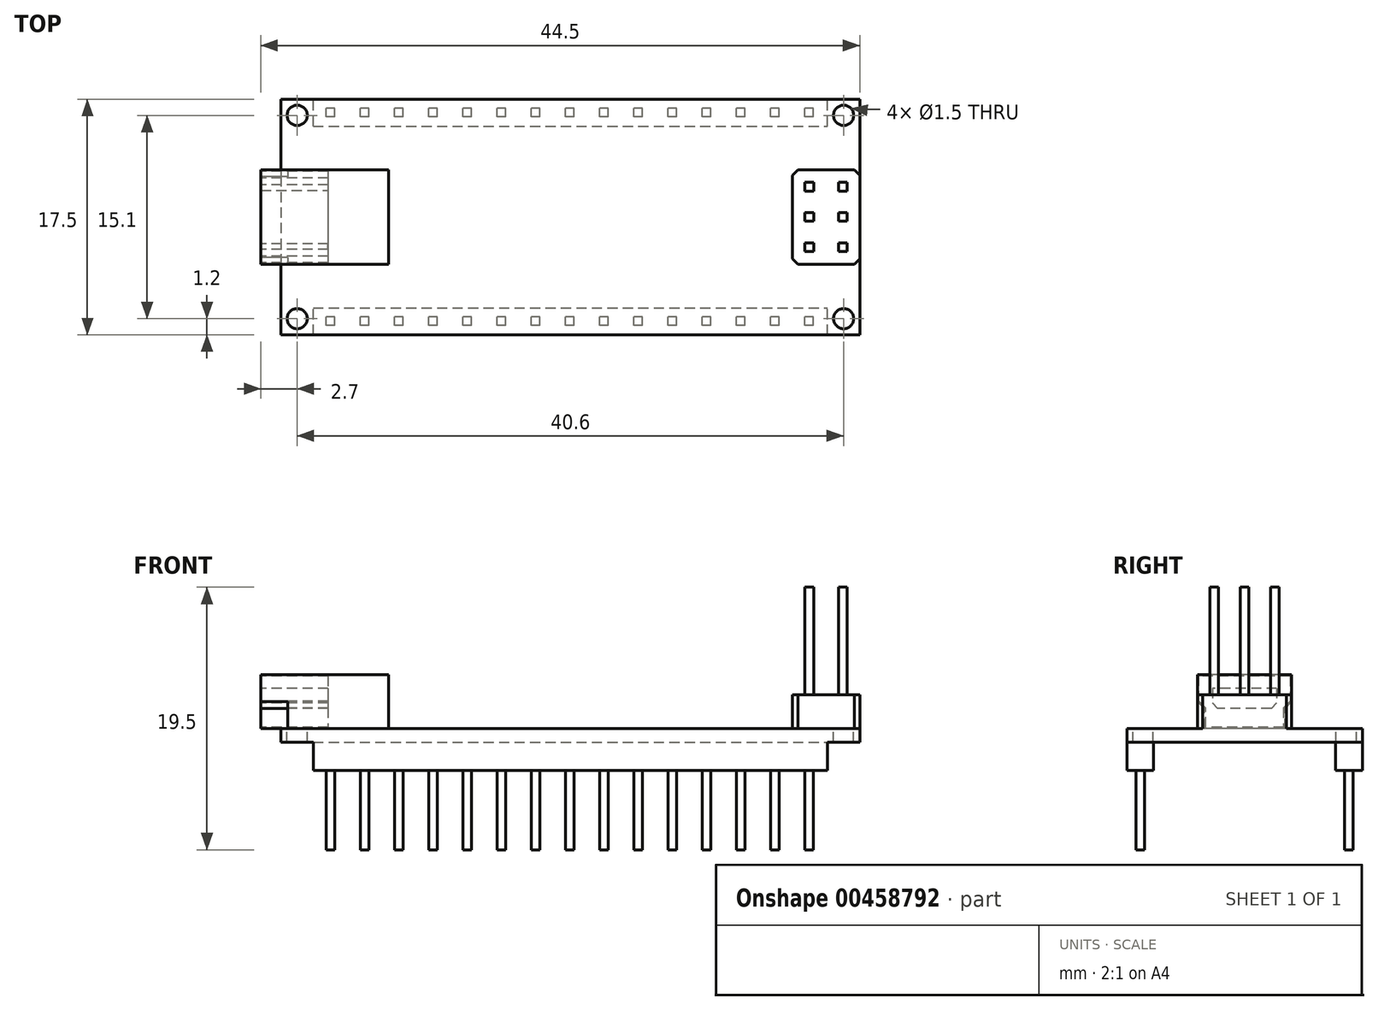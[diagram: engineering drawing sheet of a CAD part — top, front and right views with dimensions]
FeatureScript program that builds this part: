
annotation { "Feature Type Name" : "Feature", "Feature Type Description" : "" }
export const myFeature = defineFeature(function(context is Context, id is Id, definition is map)
    precondition{}
    {
        {
            var Q0;
            Q0=qCreatedBy(makeId("Top.planeOp"),FACE);
            var sketch = newSketch(context, id + "F0", { "sketchPlane" : qUnion([Q0])});
            skLineSegment(sketch, "E0.bottom", {"start": v(21.5, 8.75) * mm, "end": v(-21.5, 8.75) * mm});
            skLineSegment(sketch, "E0.top", {"start": v(21.5, -8.75) * mm, "end": v(-21.5, -8.75) * mm});
            skLineSegment(sketch, "E0.left", {"start": v(21.5, 8.75) * mm, "end": v(21.5, -8.75) * mm});
            skLineSegment(sketch, "E0.right", {"start": v(-21.5, 8.75) * mm, "end": v(-21.5, -8.75) * mm});
            skPoint(sketch, "E0.middle", {"position": v(0, 0) * mm});
            skCircle(sketch, "E1", {"center": v(-20.3, 7.55) * mm, "radius": 0.75 * mm});
            skCircle(sketch, "E2.0.1.0", {"center": v(-20.3, -7.55) * mm, "radius": 0.75 * mm});
            skCircle(sketch, "E2.1.0.0", {"center": v(20.3, 7.55) * mm, "radius": 0.75 * mm});
            skCircle(sketch, "E2.1.1.0", {"center": v(20.3, -7.55) * mm, "radius": 0.75 * mm});
            skLineSegment(sketch, "E2.direction1", {"start": v(-20.3, 7.55) * mm, "end": v(20.3, 7.55) * mm, "construction": true});
            skLineSegment(sketch, "E2.direction2", {"start": v(-20.3, 7.55) * mm, "end": v(-20.3, -7.55) * mm, "construction": true});
            skPoint(sketch, "E3", {"position": v(21.5, 0) * mm});
            skPoint(sketch, "E4", {"position": v(-21.5, 0) * mm});
            skLineSegment(sketch, "E5.bottom", {"start": v(-23, 3.5) * mm, "end": v(-13.5, 3.5) * mm});
            skLineSegment(sketch, "E5.top", {"start": v(-23, -3.5) * mm, "end": v(-13.5, -3.5) * mm});
            skLineSegment(sketch, "E5.left", {"start": v(-23, 3.5) * mm, "end": v(-23, -3.5) * mm});
            skLineSegment(sketch, "E5.right", {"start": v(-13.5, 3.5) * mm, "end": v(-13.5, -3.5) * mm});
            skPoint(sketch, "E6", {"position": v(-13.5, 0) * mm});
            skLineSegment(sketch, "E7.bottom", {"start": v(21.5, 3.5) * mm, "end": v(16.5, 3.5) * mm});
            skLineSegment(sketch, "E7.top", {"start": v(21.5, -3.5) * mm, "end": v(16.5, -3.5) * mm});
            skLineSegment(sketch, "E7.left", {"start": v(21.5, 3.5) * mm, "end": v(21.5, -3.5) * mm});
            skLineSegment(sketch, "E7.right", {"start": v(16.5, 3.5) * mm, "end": v(16.5, -3.5) * mm});
            skSolve(sketch);
        }
        {
            var Q0;
            {var subQ5=sQuery(id+"F0.wireOp",EDGE,"E5.right");Q0=makeQuery(id+"F0.imprint","IMPRINT",FACE,{"disambiguationData":[TD([[makeQuery(id+"F0.imprint","IMPRINT",EDGE,{"derivedFrom":subQ5}),-1.0]])]});}
            var Q1;
            {var subQ0=sQuery(id+"F0.wireOp",EDGE,"E0.bottom");Q1=makeQuery(id+"F0.imprint","IMPRINT",FACE,{"disambiguationData":[TD([[makeQuery(id+"F0.imprint","IMPRINT",EDGE,{"derivedFrom":subQ0}),1.0]])]});}
            var Q2;
            Q2=makeQuery(id+"F0.imprint","IMPRINT",FACE,{"disambiguationData":[TD([[makeQuery(id+"F0.imprint","IMPRINT",EDGE,{"derivedFrom":sQuery(id+"F0.wireOp",EDGE,"E7.bottom")}),1.0]])]});
            extrude(context, id + "F1", {"entities" : qUnion([Q0, Q1, Q2]), "oppositeDirection" : true, "depth" : 1 * mm});
        }
        {
            var Q0;
            {var subQ5=sQuery(id+"F0.wireOp",EDGE,"E5.left");Q0=makeQuery(id+"F0.imprint","IMPRINT",FACE,{"disambiguationData":[TD([[makeQuery(id+"F0.imprint","IMPRINT",EDGE,{"derivedFrom":subQ5}),1.0]])]});}
            var Q1;
            {var subQ5=sQuery(id+"F0.wireOp",EDGE,"E5.right");Q1=makeQuery(id+"F0.imprint","IMPRINT",FACE,{"disambiguationData":[TD([[makeQuery(id+"F0.imprint","IMPRINT",EDGE,{"derivedFrom":subQ5}),-1.0]])]});}
            extrude(context, id + "F2", {"entities" : qUnion([Q0, Q1]), "operationType" : NewBodyOperationType.ADD, "depth" : 4 * mm});
        }
        {
            var Q0;
            Q0=makeQuery(id+"F0.imprint","IMPRINT",FACE,{"disambiguationData":[TD([[makeQuery(id+"F0.imprint","IMPRINT",EDGE,{"derivedFrom":sQuery(id+"F0.wireOp",EDGE,"E7.bottom")}),1.0]])]});
            extrude(context, id + "F3", {"entities" : qUnion([Q0]), "operationType" : NewBodyOperationType.ADD, "depth" : 2.5 * mm});
        }
        {
            var Q0;
            Q0=makeQuery(id+"F2.opExtrude","SWEPT_FACE",FACE,{"disambiguationData":[OSD([sQuery(id+"F0.wireOp",EDGE,"E5.left")])]});
            var sketch = newSketch(context, id + "F4", { "sketchPlane" : qUnion([Q0])});
            skPoint(sketch, "E8", {"position": v(-3.5, 2) * mm});
            skPoint(sketch, "E9", {"position": v(3.5, 2) * mm});
            skPoint(sketch, "E10", {"position": v(-3, 0) * mm});
            skPoint(sketch, "E11", {"position": v(3, 0) * mm});
            skPoint(sketch, "E12", {"position": v(-3, 1.5) * mm});
            skPoint(sketch, "E13", {"position": v(3, 1.5) * mm});
            skLineSegment(sketch, "E14", {"start": v(-3.5, 2) * mm, "end": v(-3, 1.5) * mm});
            skLineSegment(sketch, "E15", {"start": v(-3, 0) * mm, "end": v(-3, 1.5) * mm});
            skLineSegment(sketch, "E16", {"start": v(3, 0) * mm, "end": v(3, 1.5) * mm});
            skLineSegment(sketch, "E17", {"start": v(3, 1.5) * mm, "end": v(3.5, 2) * mm});
            skLineSegment(sketch, "E18.bottom", {"start": v(-2.4, 3) * mm, "end": v(2.4, 3) * mm});
            skLineSegment(sketch, "E18.top", {"start": v(-2.4, 1.5) * mm, "end": v(2.4, 1.5) * mm});
            skLineSegment(sketch, "E18.left", {"start": v(-2.4, 3) * mm, "end": v(-2.4, 1.5) * mm});
            skLineSegment(sketch, "E18.right", {"start": v(2.4, 3) * mm, "end": v(2.4, 1.5) * mm});
            skPoint(sketch, "E19", {"position": v(0, 3) * mm});
            skPoint(sketch, "E20", {"position": v(-2.4, 2.25) * mm});
            skPoint(sketch, "E21", {"position": v(-3.5, 4) * mm});
            skPoint(sketch, "E22", {"position": v(3.5, 4) * mm});
            skLineSegment(sketch, "E23.0", {"start": v(-3.5, -1) * mm, "end": v(3.5, -1) * mm});
            skLineSegment(sketch, "E24", {"start": v(-3.5, 4) * mm, "end": v(-3.5, 2) * mm});
            skLineSegment(sketch, "E25", {"start": v(-3, 1.5) * mm, "end": v(-3, 0) * mm});
            skLineSegment(sketch, "E26", {"start": v(-3, 0) * mm, "end": v(3, 0) * mm});
            skLineSegment(sketch, "E27", {"start": v(3.5, 2) * mm, "end": v(3.5, 4) * mm});
            skLineSegment(sketch, "E28.0", {"start": v(-3.4, 3.9) * mm, "end": v(3.4, 3.9) * mm});
            skLineSegment(sketch, "E28.1", {"start": v(3.4, 2.04) * mm, "end": v(3.4, 3.9) * mm});
            skLineSegment(sketch, "E28.2", {"start": v(-3.4, 3.9) * mm, "end": v(-3.4, 2.04) * mm});
            skLineSegment(sketch, "E28.3", {"start": v(2.9, 1.54) * mm, "end": v(3.4, 2.04) * mm});
            skLineSegment(sketch, "E28.4", {"start": v(-3.4, 2.04) * mm, "end": v(-2.9, 1.54) * mm});
            skLineSegment(sketch, "E28.5", {"start": v(-2.9, 1.54) * mm, "end": v(-2.9, 0.1) * mm});
            skLineSegment(sketch, "E28.6", {"start": v(-2.9, 0.1) * mm, "end": v(2.9, 0.1) * mm});
            skLineSegment(sketch, "E28.7", {"start": v(2.9, 0.1) * mm, "end": v(2.9, 1.54) * mm});
            skPoint(sketch, "E29", {"position": v(-3.4, 2.04) * mm});
            skPoint(sketch, "E30", {"position": v(-2.9, 1.54) * mm});
            skSolve(sketch);
        }
        {
            var Q0;
            Q0=makeQuery(id+"F4.imprint","IMPRINT",FACE,{"disambiguationData":[TD([[makeQuery(id+"F4.imprint","IMPRINT",EDGE,{"derivedFrom":sQuery(id+"F4.wireOp",EDGE,"E18.bottom")}),1.0]])]});
            extrude(context, id + "F5", {"entities" : qUnion([Q0]), "operationType" : NewBodyOperationType.REMOVE, "oppositeDirection" : true, "depth" : 5 * mm});
        }
        {
            var Q0;
            {var subQ0=sQuery(id+"F4.wireOp",EDGE,"E14");Q0=makeQuery(id+"F4.imprint","IMPRINT",FACE,{"disambiguationData":[TD([[makeQuery(id+"F4.imprint","IMPRINT",EDGE,{"derivedFrom":subQ0}),-1.0]])]});}
            var Q1;
            {var subQ0=sQuery(id+"F4.wireOp",EDGE,"E16");Q1=makeQuery(id+"F4.imprint","IMPRINT",FACE,{"disambiguationData":[TD([[makeQuery(id+"F4.imprint","IMPRINT",EDGE,{"derivedFrom":subQ0}),-1.0]])]});}
            extrude(context, id + "F6", {"entities" : qUnion([Q0, Q1]), "operationType" : NewBodyOperationType.REMOVE, "oppositeDirection" : true, "depth" : 2 * mm});
        }
        {
            var Q0;
            Q0=makeQuery(id+"F1.opExtrude","CAP_FACE",FACE,{"disambiguationData":[OSD([sQuery(id+"F0.wireOp",EDGE,"E0.bottom"),sQuery(id+"F0.wireOp",EDGE,"E0.top"),sQuery(id+"F0.wireOp",EDGE,"E0.left"),sQuery(id+"F0.wireOp",EDGE,"E0.right"),sQuery(id+"F0.wireOp",EDGE,"E1"),sQuery(id+"F0.wireOp",EDGE,"E2.0.1.0"),sQuery(id+"F0.wireOp",EDGE,"E2.1.0.0"),sQuery(id+"F0.wireOp",EDGE,"E2.1.1.0"),sQuery(id+"F0.wireOp",EDGE,"E7.left")])],"isStart":false});
            var sketch = newSketch(context, id + "F7", { "sketchPlane" : qUnion([Q0])});
            skLineSegment(sketch, "E31.bottom", {"start": v(-19.1, 8.75) * mm, "end": v(19.1, 8.75) * mm});
            skLineSegment(sketch, "E31.top", {"start": v(-19.1, 6.75) * mm, "end": v(19.1, 6.75) * mm});
            skLineSegment(sketch, "E31.left", {"start": v(-19.1, 8.75) * mm, "end": v(-19.1, 6.75) * mm});
            skLineSegment(sketch, "E31.right", {"start": v(19.1, 8.75) * mm, "end": v(19.1, 6.75) * mm});
            skPoint(sketch, "E32", {"position": v(0, 6.75) * mm});
            skLineSegment(sketch, "E33", {"start": v(-19.1, 7.75) * mm, "end": v(19.1, 7.75) * mm, "construction": true});
            skPoint(sketch, "E34", {"position": v(-17.83, 7.75) * mm});
            skLineSegment(sketch, "E35.bottom", {"start": v(-17.51, 8.07) * mm, "end": v(-18.15, 8.07) * mm});
            skLineSegment(sketch, "E35.top", {"start": v(-17.51, 7.43) * mm, "end": v(-18.15, 7.43) * mm});
            skLineSegment(sketch, "E35.left", {"start": v(-17.51, 8.07) * mm, "end": v(-17.51, 7.43) * mm});
            skLineSegment(sketch, "E35.right", {"start": v(-18.15, 8.07) * mm, "end": v(-18.15, 7.43) * mm});
            skPoint(sketch, "E36.1.0.0", {"position": v(-15.3, 7.75) * mm});
            skLineSegment(sketch, "E36.1.0.1", {"start": v(-14.97, 8.07) * mm, "end": v(-14.97, 7.43) * mm});
            skLineSegment(sketch, "E36.1.0.2", {"start": v(-14.97, 8.07) * mm, "end": v(-15.61, 8.07) * mm});
            skLineSegment(sketch, "E36.1.0.3", {"start": v(-15.61, 8.07) * mm, "end": v(-15.61, 7.43) * mm});
            skLineSegment(sketch, "E36.1.0.4", {"start": v(-14.97, 7.43) * mm, "end": v(-15.61, 7.43) * mm});
            skPoint(sketch, "E36.2.0.0", {"position": v(-12.75, 7.75) * mm});
            skLineSegment(sketch, "E36.2.0.1", {"start": v(-12.43, 8.07) * mm, "end": v(-12.43, 7.43) * mm});
            skLineSegment(sketch, "E36.2.0.2", {"start": v(-12.43, 8.07) * mm, "end": v(-13.07, 8.07) * mm});
            skLineSegment(sketch, "E36.2.0.3", {"start": v(-13.07, 8.07) * mm, "end": v(-13.07, 7.43) * mm});
            skLineSegment(sketch, "E36.2.0.4", {"start": v(-12.43, 7.43) * mm, "end": v(-13.07, 7.43) * mm});
            skPoint(sketch, "E36.3.0.0", {"position": v(-10.21, 7.75) * mm});
            skLineSegment(sketch, "E36.3.0.1", {"start": v(-9.89, 8.07) * mm, "end": v(-9.89, 7.43) * mm});
            skLineSegment(sketch, "E36.3.0.2", {"start": v(-9.89, 8.07) * mm, "end": v(-10.53, 8.07) * mm});
            skLineSegment(sketch, "E36.3.0.3", {"start": v(-10.53, 8.07) * mm, "end": v(-10.53, 7.43) * mm});
            skLineSegment(sketch, "E36.3.0.4", {"start": v(-9.89, 7.43) * mm, "end": v(-10.53, 7.43) * mm});
            skPoint(sketch, "E36.4.0.0", {"position": v(-7.67, 7.75) * mm});
            skLineSegment(sketch, "E36.4.0.1", {"start": v(-7.35, 8.07) * mm, "end": v(-7.35, 7.43) * mm});
            skLineSegment(sketch, "E36.4.0.2", {"start": v(-7.35, 8.07) * mm, "end": v(-8, 8.07) * mm});
            skLineSegment(sketch, "E36.4.0.3", {"start": v(-8, 8.07) * mm, "end": v(-8, 7.43) * mm});
            skLineSegment(sketch, "E36.4.0.4", {"start": v(-7.35, 7.43) * mm, "end": v(-8, 7.43) * mm});
            skPoint(sketch, "E36.5.0.0", {"position": v(-5.13, 7.75) * mm});
            skLineSegment(sketch, "E36.5.0.1", {"start": v(-4.8, 8.07) * mm, "end": v(-4.8, 7.43) * mm});
            skLineSegment(sketch, "E36.5.0.2", {"start": v(-4.8, 8.07) * mm, "end": v(-5.45, 8.07) * mm});
            skLineSegment(sketch, "E36.5.0.3", {"start": v(-5.45, 8.07) * mm, "end": v(-5.45, 7.43) * mm});
            skLineSegment(sketch, "E36.5.0.4", {"start": v(-4.8, 7.43) * mm, "end": v(-5.45, 7.43) * mm});
            skPoint(sketch, "E36.6.0.0", {"position": v(-2.59, 7.75) * mm});
            skLineSegment(sketch, "E36.6.0.1", {"start": v(-2.27, 8.07) * mm, "end": v(-2.27, 7.43) * mm});
            skLineSegment(sketch, "E36.6.0.2", {"start": v(-2.27, 8.07) * mm, "end": v(-2.9, 8.07) * mm});
            skLineSegment(sketch, "E36.6.0.3", {"start": v(-2.9, 8.07) * mm, "end": v(-2.9, 7.43) * mm});
            skLineSegment(sketch, "E36.6.0.4", {"start": v(-2.27, 7.43) * mm, "end": v(-2.9, 7.43) * mm});
            skPoint(sketch, "E36.7.0.0", {"position": v(-0.05, 7.75) * mm});
            skLineSegment(sketch, "E36.7.0.1", {"start": v(0.27, 8.07) * mm, "end": v(0.27, 7.43) * mm});
            skLineSegment(sketch, "E36.7.0.2", {"start": v(0.27, 8.07) * mm, "end": v(-0.37, 8.07) * mm});
            skLineSegment(sketch, "E36.7.0.3", {"start": v(-0.37, 8.07) * mm, "end": v(-0.37, 7.43) * mm});
            skLineSegment(sketch, "E36.7.0.4", {"start": v(0.27, 7.43) * mm, "end": v(-0.37, 7.43) * mm});
            skPoint(sketch, "E36.8.0.0", {"position": v(2.5, 7.75) * mm});
            skLineSegment(sketch, "E36.8.0.1", {"start": v(2.81, 8.07) * mm, "end": v(2.81, 7.43) * mm});
            skLineSegment(sketch, "E36.8.0.2", {"start": v(2.81, 8.07) * mm, "end": v(2.17, 8.07) * mm});
            skLineSegment(sketch, "E36.8.0.3", {"start": v(2.17, 8.07) * mm, "end": v(2.17, 7.43) * mm});
            skLineSegment(sketch, "E36.8.0.4", {"start": v(2.81, 7.43) * mm, "end": v(2.17, 7.43) * mm});
            skPoint(sketch, "E36.9.0.0", {"position": v(5.03, 7.75) * mm});
            skLineSegment(sketch, "E36.9.0.1", {"start": v(5.35, 8.07) * mm, "end": v(5.35, 7.43) * mm});
            skLineSegment(sketch, "E36.9.0.2", {"start": v(5.35, 8.07) * mm, "end": v(4.71, 8.07) * mm});
            skLineSegment(sketch, "E36.9.0.3", {"start": v(4.71, 8.07) * mm, "end": v(4.71, 7.43) * mm});
            skLineSegment(sketch, "E36.9.0.4", {"start": v(5.35, 7.43) * mm, "end": v(4.71, 7.43) * mm});
            skPoint(sketch, "E36.10.0.0", {"position": v(7.57, 7.75) * mm});
            skLineSegment(sketch, "E36.10.0.1", {"start": v(7.9, 8.07) * mm, "end": v(7.9, 7.43) * mm});
            skLineSegment(sketch, "E36.10.0.2", {"start": v(7.9, 8.07) * mm, "end": v(7.25, 8.07) * mm});
            skLineSegment(sketch, "E36.10.0.3", {"start": v(7.25, 8.07) * mm, "end": v(7.25, 7.43) * mm});
            skLineSegment(sketch, "E36.10.0.4", {"start": v(7.9, 7.43) * mm, "end": v(7.25, 7.43) * mm});
            skPoint(sketch, "E36.11.0.0", {"position": v(10.11, 7.75) * mm});
            skLineSegment(sketch, "E36.11.0.1", {"start": v(10.43, 8.07) * mm, "end": v(10.43, 7.43) * mm});
            skLineSegment(sketch, "E36.11.0.2", {"start": v(10.43, 8.07) * mm, "end": v(9.8, 8.07) * mm});
            skLineSegment(sketch, "E36.11.0.3", {"start": v(9.8, 8.07) * mm, "end": v(9.8, 7.43) * mm});
            skLineSegment(sketch, "E36.11.0.4", {"start": v(10.43, 7.43) * mm, "end": v(9.8, 7.43) * mm});
            skPoint(sketch, "E36.12.0.0", {"position": v(12.65, 7.75) * mm});
            skLineSegment(sketch, "E36.12.0.1", {"start": v(12.97, 8.07) * mm, "end": v(12.97, 7.43) * mm});
            skLineSegment(sketch, "E36.12.0.2", {"start": v(12.97, 8.07) * mm, "end": v(12.33, 8.07) * mm});
            skLineSegment(sketch, "E36.12.0.3", {"start": v(12.33, 8.07) * mm, "end": v(12.33, 7.43) * mm});
            skLineSegment(sketch, "E36.12.0.4", {"start": v(12.97, 7.43) * mm, "end": v(12.33, 7.43) * mm});
            skPoint(sketch, "E36.13.0.0", {"position": v(15.2, 7.75) * mm});
            skLineSegment(sketch, "E36.13.0.1", {"start": v(15.51, 8.07) * mm, "end": v(15.51, 7.43) * mm});
            skLineSegment(sketch, "E36.13.0.2", {"start": v(15.51, 8.07) * mm, "end": v(14.87, 8.07) * mm});
            skLineSegment(sketch, "E36.13.0.3", {"start": v(14.87, 8.07) * mm, "end": v(14.87, 7.43) * mm});
            skLineSegment(sketch, "E36.13.0.4", {"start": v(15.51, 7.43) * mm, "end": v(14.87, 7.43) * mm});
            skPoint(sketch, "E36.14.0.0", {"position": v(17.73, 7.75) * mm});
            skLineSegment(sketch, "E36.14.0.1", {"start": v(18.05, 8.07) * mm, "end": v(18.05, 7.43) * mm});
            skLineSegment(sketch, "E36.14.0.2", {"start": v(18.05, 8.07) * mm, "end": v(17.41, 8.07) * mm});
            skLineSegment(sketch, "E36.14.0.3", {"start": v(17.41, 8.07) * mm, "end": v(17.41, 7.43) * mm});
            skLineSegment(sketch, "E36.14.0.4", {"start": v(18.05, 7.43) * mm, "end": v(17.41, 7.43) * mm});
            skLineSegment(sketch, "E36.direction1", {"start": v(-17.83, 7.75) * mm, "end": v(-15.3, 7.75) * mm, "construction": true});
            skPoint(sketch, "E37", {"position": v(-20.3, 7.55) * mm});
            skLineSegment(sketch, "E38", {"start": v(-20.3, 7.55) * mm, "end": v(-21.5, 7.55) * mm});
            skLineSegment(sketch, "E39", {"start": v(-21.5, 7.55) * mm, "end": v(-19.1, 7.55) * mm});
            skPoint(sketch, "E40", {"position": v(-21.05, 7.55) * mm});
            skPoint(sketch, "E41", {"position": v(-19.55, 7.55) * mm});
            skPoint(sketch, "E42", {"position": v(20.3, 7.55) * mm});
            skLineSegment(sketch, "E43", {"start": v(20.3, 7.55) * mm, "end": v(21.5, 7.55) * mm});
            skLineSegment(sketch, "E44", {"start": v(21.5, 7.55) * mm, "end": v(19.1, 7.55) * mm});
            skPoint(sketch, "E45", {"position": v(21.05, 7.55) * mm});
            skPoint(sketch, "E46", {"position": v(19.55, 7.55) * mm});
            skPoint(sketch, "E47.0.1.0", {"position": v(-0.05, -7.75) * mm});
            skPoint(sketch, "E47.0.1.1", {"position": v(-5.13, -7.75) * mm});
            skPoint(sketch, "E47.0.1.2", {"position": v(12.65, -7.75) * mm});
            skPoint(sketch, "E47.0.1.3", {"position": v(-7.67, -7.75) * mm});
            skPoint(sketch, "E47.0.1.4", {"position": v(17.73, -7.75) * mm});
            skPoint(sketch, "E47.0.1.5", {"position": v(-10.21, -7.75) * mm});
            skPoint(sketch, "E47.0.1.6", {"position": v(7.57, -7.75) * mm});
            skPoint(sketch, "E47.0.1.7", {"position": v(2.49, -7.75) * mm});
            skPoint(sketch, "E47.0.1.8", {"position": v(0, -8.75) * mm});
            skPoint(sketch, "E47.0.1.9", {"position": v(-17.83, -7.75) * mm});
            skPoint(sketch, "E47.0.1.10", {"position": v(5.03, -7.75) * mm});
            skPoint(sketch, "E47.0.1.11", {"position": v(-15.3, -7.75) * mm});
            skLineSegment(sketch, "E47.0.1.12", {"start": v(-17.83, -7.75) * mm, "end": v(-15.3, -7.75) * mm, "construction": true});
            skPoint(sketch, "E47.0.1.13", {"position": v(10.11, -7.75) * mm});
            skPoint(sketch, "E47.0.1.14", {"position": v(15.2, -7.75) * mm});
            skPoint(sketch, "E47.0.1.15", {"position": v(-2.6, -7.75) * mm});
            skPoint(sketch, "E47.0.1.16", {"position": v(-12.75, -7.75) * mm});
            skPoint(sketch, "E47.0.1.17", {"position": v(-17.83, -7.75) * mm});
            skLineSegment(sketch, "E47.0.1.18", {"start": v(18.05, -7.43) * mm, "end": v(17.41, -7.43) * mm});
            skLineSegment(sketch, "E47.0.1.19", {"start": v(18.05, -8.07) * mm, "end": v(17.41, -8.07) * mm});
            skLineSegment(sketch, "E47.0.1.20", {"start": v(18.05, -7.43) * mm, "end": v(18.05, -8.07) * mm});
            skLineSegment(sketch, "E47.0.1.21", {"start": v(-0.37, -7.43) * mm, "end": v(-0.37, -8.07) * mm});
            skLineSegment(sketch, "E47.0.1.22", {"start": v(-10.53, -7.43) * mm, "end": v(-10.53, -8.07) * mm});
            skLineSegment(sketch, "E47.0.1.23", {"start": v(-9.89, -7.43) * mm, "end": v(-10.53, -7.43) * mm});
            skLineSegment(sketch, "E47.0.1.24", {"start": v(-2.27, -7.43) * mm, "end": v(-2.9, -7.43) * mm});
            skLineSegment(sketch, "E47.0.1.25", {"start": v(12.97, -7.43) * mm, "end": v(12.97, -8.07) * mm});
            skLineSegment(sketch, "E47.0.1.26", {"start": v(-5.45, -7.43) * mm, "end": v(-5.45, -8.07) * mm});
            skLineSegment(sketch, "E47.0.1.27", {"start": v(-7.35, -8.07) * mm, "end": v(-7.99, -8.07) * mm});
            skLineSegment(sketch, "E47.0.1.28", {"start": v(2.81, -8.07) * mm, "end": v(2.17, -8.07) * mm});
            skLineSegment(sketch, "E47.0.1.29", {"start": v(12.97, -8.07) * mm, "end": v(12.33, -8.07) * mm});
            skLineSegment(sketch, "E47.0.1.30", {"start": v(7.9, -8.07) * mm, "end": v(7.25, -8.07) * mm});
            skLineSegment(sketch, "E47.0.1.31", {"start": v(7.25, -7.43) * mm, "end": v(7.25, -8.07) * mm});
            skLineSegment(sketch, "E47.0.1.32", {"start": v(-2.9, -7.43) * mm, "end": v(-2.9, -8.07) * mm});
            skLineSegment(sketch, "E47.0.1.33", {"start": v(-7.35, -7.43) * mm, "end": v(-7.99, -7.43) * mm});
            skLineSegment(sketch, "E47.0.1.34", {"start": v(2.81, -7.43) * mm, "end": v(2.81, -8.07) * mm});
            skLineSegment(sketch, "E47.0.1.35", {"start": v(7.9, -7.43) * mm, "end": v(7.25, -7.43) * mm});
            skLineSegment(sketch, "E47.0.1.36", {"start": v(-4.8, -8.07) * mm, "end": v(-5.45, -8.07) * mm});
            skLineSegment(sketch, "E47.0.1.37", {"start": v(-7.35, -7.43) * mm, "end": v(-7.35, -8.07) * mm});
            skLineSegment(sketch, "E47.0.1.38", {"start": v(15.5, -8.07) * mm, "end": v(14.87, -8.07) * mm});
            skLineSegment(sketch, "E47.0.1.39", {"start": v(5.35, -8.07) * mm, "end": v(4.71, -8.07) * mm});
            skLineSegment(sketch, "E47.0.1.40", {"start": v(-2.27, -8.07) * mm, "end": v(-2.9, -8.07) * mm});
            skLineSegment(sketch, "E47.0.1.41", {"start": v(-12.43, -8.07) * mm, "end": v(-13.07, -8.07) * mm});
            skLineSegment(sketch, "E47.0.1.42", {"start": v(2.81, -7.43) * mm, "end": v(2.17, -7.43) * mm});
            skLineSegment(sketch, "E47.0.1.43", {"start": v(17.41, -7.43) * mm, "end": v(17.41, -8.07) * mm});
            skLineSegment(sketch, "E47.0.1.44", {"start": v(12.97, -7.43) * mm, "end": v(12.33, -7.43) * mm});
            skLineSegment(sketch, "E47.0.1.45", {"start": v(7.9, -7.43) * mm, "end": v(7.9, -8.07) * mm});
            skLineSegment(sketch, "E47.0.1.46", {"start": v(-2.27, -7.43) * mm, "end": v(-2.27, -8.07) * mm});
            skLineSegment(sketch, "E47.0.1.47", {"start": v(-17.5, -8.07) * mm, "end": v(-18.15, -8.07) * mm});
            skLineSegment(sketch, "E47.0.1.48", {"start": v(12.33, -7.43) * mm, "end": v(12.33, -8.07) * mm});
            skLineSegment(sketch, "E47.0.1.49", {"start": v(-14.97, -7.43) * mm, "end": v(-14.97, -8.07) * mm});
            skLineSegment(sketch, "E47.0.1.50", {"start": v(2.17, -7.43) * mm, "end": v(2.17, -8.07) * mm});
            skLineSegment(sketch, "E47.0.1.51", {"start": v(-8, -7.43) * mm, "end": v(-8, -8.07) * mm});
            skLineSegment(sketch, "E47.0.1.52", {"start": v(-14.97, -7.43) * mm, "end": v(-15.6, -7.43) * mm});
            skLineSegment(sketch, "E47.0.1.53", {"start": v(-15.61, -7.43) * mm, "end": v(-15.61, -8.07) * mm});
            skLineSegment(sketch, "E47.0.1.54", {"start": v(-14.97, -8.07) * mm, "end": v(-15.6, -8.07) * mm});
            skLineSegment(sketch, "E47.0.1.55", {"start": v(-9.89, -7.43) * mm, "end": v(-9.89, -8.07) * mm});
            skLineSegment(sketch, "E47.0.1.56", {"start": v(0.27, -7.43) * mm, "end": v(0.27, -8.07) * mm});
            skLineSegment(sketch, "E47.0.1.57", {"start": v(10.43, -7.43) * mm, "end": v(10.43, -8.07) * mm});
            skLineSegment(sketch, "E47.0.1.58", {"start": v(-12.43, -7.43) * mm, "end": v(-12.43, -8.07) * mm});
            skLineSegment(sketch, "E47.0.1.59", {"start": v(10.43, -7.43) * mm, "end": v(9.8, -7.43) * mm});
            skLineSegment(sketch, "E47.0.1.60", {"start": v(0.27, -7.43) * mm, "end": v(-0.37, -7.43) * mm});
            skLineSegment(sketch, "E47.0.1.61", {"start": v(15.51, -7.43) * mm, "end": v(15.51, -8.07) * mm});
            skLineSegment(sketch, "E47.0.1.62", {"start": v(5.35, -7.43) * mm, "end": v(5.35, -8.07) * mm});
            skLineSegment(sketch, "E47.0.1.63", {"start": v(-4.8, -7.43) * mm, "end": v(-4.8, -8.07) * mm});
            skLineSegment(sketch, "E47.0.1.64", {"start": v(15.51, -7.43) * mm, "end": v(14.87, -7.43) * mm});
            skLineSegment(sketch, "E47.0.1.65", {"start": v(5.35, -7.43) * mm, "end": v(4.71, -7.43) * mm});
            skLineSegment(sketch, "E47.0.1.66", {"start": v(-4.8, -7.43) * mm, "end": v(-5.45, -7.43) * mm});
            skLineSegment(sketch, "E47.0.1.67", {"start": v(10.43, -8.07) * mm, "end": v(9.8, -8.07) * mm});
            skLineSegment(sketch, "E47.0.1.68", {"start": v(0.27, -8.07) * mm, "end": v(-0.37, -8.07) * mm});
            skLineSegment(sketch, "E47.0.1.69", {"start": v(-9.9, -8.07) * mm, "end": v(-10.53, -8.07) * mm});
            skLineSegment(sketch, "E47.0.1.70", {"start": v(4.71, -7.43) * mm, "end": v(4.71, -8.07) * mm});
            skLineSegment(sketch, "E47.0.1.71", {"start": v(14.87, -7.43) * mm, "end": v(14.87, -8.07) * mm});
            skLineSegment(sketch, "E47.0.1.72", {"start": v(9.8, -7.43) * mm, "end": v(9.8, -8.07) * mm});
            skLineSegment(sketch, "E47.0.1.73", {"start": v(-12.43, -7.43) * mm, "end": v(-13.07, -7.43) * mm});
            skLineSegment(sketch, "E47.0.1.74", {"start": v(-13.07, -7.43) * mm, "end": v(-13.07, -8.07) * mm});
            skLineSegment(sketch, "E47.0.1.75", {"start": v(-18.15, -7.43) * mm, "end": v(-18.15, -8.07) * mm});
            skLineSegment(sketch, "E47.0.1.76", {"start": v(-17.51, -7.43) * mm, "end": v(-17.51, -8.07) * mm});
            skLineSegment(sketch, "E47.0.1.77", {"start": v(-17.5, -7.43) * mm, "end": v(-18.15, -7.43) * mm});
            skLineSegment(sketch, "E47.0.1.78", {"start": v(19.1, -6.75) * mm, "end": v(19.1, -8.75) * mm});
            skLineSegment(sketch, "E47.0.1.79", {"start": v(-19.1, -8.75) * mm, "end": v(19.1, -8.75) * mm});
            skLineSegment(sketch, "E47.0.1.80", {"start": v(-19.1, -6.75) * mm, "end": v(-19.1, -8.75) * mm});
            skLineSegment(sketch, "E47.0.1.81", {"start": v(-19.1, -6.75) * mm, "end": v(19.1, -6.75) * mm});
            skLineSegment(sketch, "E47.direction1", {"start": v(-0.05, 7.75) * mm, "end": v(24.95, 7.75) * mm, "construction": true});
            skLineSegment(sketch, "E47.direction2", {"start": v(-0.05, 7.75) * mm, "end": v(-0.05, -7.75) * mm, "construction": true});
            skSolve(sketch);
        }
        {
            var Q0;
            Q0=makeQuery(id+"F7.imprint","IMPRINT",FACE,{"disambiguationData":[TD([[makeQuery(id+"F7.imprint","IMPRINT",EDGE,{"derivedFrom":sQuery(id+"F7.wireOp",EDGE,"E47.0.1.18")}),-1.0]])]});
            var Q1;
            {var subQ1=sQuery(id+"F7.wireOp",EDGE,"E31.bottom");Q1=makeQuery(id+"F7.imprint","IMPRINT",FACE,{"disambiguationData":[TD([[makeQuery(id+"F7.imprint","IMPRINT",EDGE,{"derivedFrom":subQ1}),1.0]])]});}
            extrude(context, id + "F8", {"entities" : qUnion([Q0, Q1]), "depth" : 2.1 * mm, "offsetDistance" : 25 * mm});
        }
        {
            var Q0;
            Q0=makeQuery(id+"F7.imprint","IMPRINT",FACE,{"disambiguationData":[TD([[makeQuery(id+"F7.imprint","IMPRINT",EDGE,{"derivedFrom":sQuery(id+"F7.wireOp",EDGE,"E35.bottom")}),1.0]])]});
            var Q1;
            Q1=makeQuery(id+"F7.imprint","IMPRINT",FACE,{"disambiguationData":[TD([[makeQuery(id+"F7.imprint","IMPRINT",EDGE,{"derivedFrom":sQuery(id+"F7.wireOp",EDGE,"E36.1.0.1")}),-1.0]])]});
            var Q2;
            Q2=makeQuery(id+"F7.imprint","IMPRINT",FACE,{"disambiguationData":[TD([[makeQuery(id+"F7.imprint","IMPRINT",EDGE,{"derivedFrom":sQuery(id+"F7.wireOp",EDGE,"E36.2.0.1")}),-1.0]])]});
            var Q3;
            Q3=makeQuery(id+"F7.imprint","IMPRINT",FACE,{"disambiguationData":[TD([[makeQuery(id+"F7.imprint","IMPRINT",EDGE,{"derivedFrom":sQuery(id+"F7.wireOp",EDGE,"E36.3.0.1")}),-1.0]])]});
            var Q4;
            Q4=makeQuery(id+"F7.imprint","IMPRINT",FACE,{"disambiguationData":[TD([[makeQuery(id+"F7.imprint","IMPRINT",EDGE,{"derivedFrom":sQuery(id+"F7.wireOp",EDGE,"E36.4.0.1")}),-1.0]])]});
            var Q5;
            Q5=makeQuery(id+"F7.imprint","IMPRINT",FACE,{"disambiguationData":[TD([[makeQuery(id+"F7.imprint","IMPRINT",EDGE,{"derivedFrom":sQuery(id+"F7.wireOp",EDGE,"E36.5.0.1")}),-1.0]])]});
            var Q6;
            Q6=makeQuery(id+"F7.imprint","IMPRINT",FACE,{"disambiguationData":[TD([[makeQuery(id+"F7.imprint","IMPRINT",EDGE,{"derivedFrom":sQuery(id+"F7.wireOp",EDGE,"E36.6.0.1")}),-1.0]])]});
            var Q7;
            Q7=makeQuery(id+"F7.imprint","IMPRINT",FACE,{"disambiguationData":[TD([[makeQuery(id+"F7.imprint","IMPRINT",EDGE,{"derivedFrom":sQuery(id+"F7.wireOp",EDGE,"E36.7.0.1")}),-1.0]])]});
            var Q8;
            Q8=makeQuery(id+"F7.imprint","IMPRINT",FACE,{"disambiguationData":[TD([[makeQuery(id+"F7.imprint","IMPRINT",EDGE,{"derivedFrom":sQuery(id+"F7.wireOp",EDGE,"E36.8.0.1")}),-1.0]])]});
            var Q9;
            Q9=makeQuery(id+"F7.imprint","IMPRINT",FACE,{"disambiguationData":[TD([[makeQuery(id+"F7.imprint","IMPRINT",EDGE,{"derivedFrom":sQuery(id+"F7.wireOp",EDGE,"E36.9.0.1")}),-1.0]])]});
            var Q10;
            Q10=makeQuery(id+"F7.imprint","IMPRINT",FACE,{"disambiguationData":[TD([[makeQuery(id+"F7.imprint","IMPRINT",EDGE,{"derivedFrom":sQuery(id+"F7.wireOp",EDGE,"E36.10.0.1")}),-1.0]])]});
            var Q11;
            Q11=makeQuery(id+"F7.imprint","IMPRINT",FACE,{"disambiguationData":[TD([[makeQuery(id+"F7.imprint","IMPRINT",EDGE,{"derivedFrom":sQuery(id+"F7.wireOp",EDGE,"E36.11.0.1")}),-1.0]])]});
            var Q12;
            Q12=makeQuery(id+"F7.imprint","IMPRINT",FACE,{"disambiguationData":[TD([[makeQuery(id+"F7.imprint","IMPRINT",EDGE,{"derivedFrom":sQuery(id+"F7.wireOp",EDGE,"E36.12.0.1")}),-1.0]])]});
            var Q13;
            Q13=makeQuery(id+"F7.imprint","IMPRINT",FACE,{"disambiguationData":[TD([[makeQuery(id+"F7.imprint","IMPRINT",EDGE,{"derivedFrom":sQuery(id+"F7.wireOp",EDGE,"E36.13.0.1")}),-1.0]])]});
            var Q14;
            Q14=makeQuery(id+"F7.imprint","IMPRINT",FACE,{"disambiguationData":[TD([[makeQuery(id+"F7.imprint","IMPRINT",EDGE,{"derivedFrom":sQuery(id+"F7.wireOp",EDGE,"E36.14.0.1")}),-1.0]])]});
            var Q15;
            Q15=makeQuery(id+"F7.imprint","IMPRINT",FACE,{"disambiguationData":[TD([[makeQuery(id+"F7.imprint","IMPRINT",EDGE,{"derivedFrom":sQuery(id+"F7.wireOp",EDGE,"E47.0.1.47")}),-1.0]])]});
            var Q16;
            Q16=makeQuery(id+"F7.imprint","IMPRINT",FACE,{"disambiguationData":[TD([[makeQuery(id+"F7.imprint","IMPRINT",EDGE,{"derivedFrom":sQuery(id+"F7.wireOp",EDGE,"E47.0.1.49")}),-1.0]])]});
            var Q17;
            Q17=makeQuery(id+"F7.imprint","IMPRINT",FACE,{"disambiguationData":[TD([[makeQuery(id+"F7.imprint","IMPRINT",EDGE,{"derivedFrom":sQuery(id+"F7.wireOp",EDGE,"E47.0.1.41")}),-1.0]])]});
            var Q18;
            Q18=makeQuery(id+"F7.imprint","IMPRINT",FACE,{"disambiguationData":[TD([[makeQuery(id+"F7.imprint","IMPRINT",EDGE,{"derivedFrom":sQuery(id+"F7.wireOp",EDGE,"E47.0.1.22")}),1.0]])]});
            var Q19;
            Q19=makeQuery(id+"F7.imprint","IMPRINT",FACE,{"disambiguationData":[TD([[makeQuery(id+"F7.imprint","IMPRINT",EDGE,{"derivedFrom":sQuery(id+"F7.wireOp",EDGE,"E47.0.1.27")}),-1.0]])]});
            var Q20;
            Q20=makeQuery(id+"F7.imprint","IMPRINT",FACE,{"disambiguationData":[TD([[makeQuery(id+"F7.imprint","IMPRINT",EDGE,{"derivedFrom":sQuery(id+"F7.wireOp",EDGE,"E47.0.1.26")}),1.0]])]});
            var Q21;
            Q21=makeQuery(id+"F7.imprint","IMPRINT",FACE,{"disambiguationData":[TD([[makeQuery(id+"F7.imprint","IMPRINT",EDGE,{"derivedFrom":sQuery(id+"F7.wireOp",EDGE,"E47.0.1.24")}),1.0]])]});
            var Q22;
            Q22=makeQuery(id+"F7.imprint","IMPRINT",FACE,{"disambiguationData":[TD([[makeQuery(id+"F7.imprint","IMPRINT",EDGE,{"derivedFrom":sQuery(id+"F7.wireOp",EDGE,"E47.0.1.21")}),1.0]])]});
            var Q23;
            Q23=makeQuery(id+"F7.imprint","IMPRINT",FACE,{"disambiguationData":[TD([[makeQuery(id+"F7.imprint","IMPRINT",EDGE,{"derivedFrom":sQuery(id+"F7.wireOp",EDGE,"E47.0.1.28")}),-1.0]])]});
            var Q24;
            Q24=makeQuery(id+"F7.imprint","IMPRINT",FACE,{"disambiguationData":[TD([[makeQuery(id+"F7.imprint","IMPRINT",EDGE,{"derivedFrom":sQuery(id+"F7.wireOp",EDGE,"E47.0.1.39")}),-1.0]])]});
            var Q25;
            Q25=makeQuery(id+"F7.imprint","IMPRINT",FACE,{"disambiguationData":[TD([[makeQuery(id+"F7.imprint","IMPRINT",EDGE,{"derivedFrom":sQuery(id+"F7.wireOp",EDGE,"E47.0.1.30")}),-1.0]])]});
            var Q26;
            Q26=makeQuery(id+"F7.imprint","IMPRINT",FACE,{"disambiguationData":[TD([[makeQuery(id+"F7.imprint","IMPRINT",EDGE,{"derivedFrom":sQuery(id+"F7.wireOp",EDGE,"E47.0.1.57")}),-1.0]])]});
            var Q27;
            Q27=makeQuery(id+"F7.imprint","IMPRINT",FACE,{"disambiguationData":[TD([[makeQuery(id+"F7.imprint","IMPRINT",EDGE,{"derivedFrom":sQuery(id+"F7.wireOp",EDGE,"E47.0.1.25")}),-1.0]])]});
            var Q28;
            Q28=makeQuery(id+"F7.imprint","IMPRINT",FACE,{"disambiguationData":[TD([[makeQuery(id+"F7.imprint","IMPRINT",EDGE,{"derivedFrom":sQuery(id+"F7.wireOp",EDGE,"E47.0.1.38")}),-1.0]])]});
            var Q29;
            Q29=makeQuery(id+"F7.imprint","IMPRINT",FACE,{"disambiguationData":[TD([[makeQuery(id+"F7.imprint","IMPRINT",EDGE,{"derivedFrom":sQuery(id+"F7.wireOp",EDGE,"E47.0.1.18")}),1.0]])]});
            extrude(context, id + "F9", {"entities" : qUnion([Q0, Q1, Q2, Q3, Q4, Q5, Q6, Q7, Q8, Q9, Q10, Q11, Q12, Q13, Q14, Q15, Q16, Q17, Q18, Q19, Q20, Q21, Q22, Q23, Q24, Q25, Q26, Q27, Q28, Q29]), "operationType" : NewBodyOperationType.ADD, "depth" : 8 * mm});
        }
        {
            var Q0;
            Q0=makeQuery(id+"F5.boolean.opBoolean","COPY",EDGE,{"derivedFrom":makeQuery(id+"F5.opExtrude","SWEPT_EDGE",EDGE,{"disambiguationData":[OSD([sQuery(id+"F4.wireOp",EDGE,"E18.top"),sQuery(id+"F4.wireOp",EDGE,"E18.right")])]})});
            var Q1;
            Q1=makeQuery(id+"F5.boolean.opBoolean","COPY",EDGE,{"derivedFrom":makeQuery(id+"F5.opExtrude","SWEPT_EDGE",EDGE,{"disambiguationData":[OSD([sQuery(id+"F4.wireOp",EDGE,"E18.top"),sQuery(id+"F4.wireOp",EDGE,"E18.left")])]})});
            chamfer(context, id + "F10", {"entities" : qUnion([Q0, Q1]), "width" : 0.4 * mm, "tangentPropagation" : true});
        }
        {
            var Q0;
            Q0=makeQuery(id+"F3.opExtrude","CAP_FACE",FACE,{"disambiguationData":[OSD([sQuery(id+"F0.wireOp",EDGE,"E7.bottom"),sQuery(id+"F0.wireOp",EDGE,"E7.top"),sQuery(id+"F0.wireOp",EDGE,"E7.left"),sQuery(id+"F0.wireOp",EDGE,"E7.right")])],"isStart":false});
            var sketch = newSketch(context, id + "F11", { "sketchPlane" : qUnion([Q0])});
            skPoint(sketch, "E48", {"position": v(21.5, 1.17) * mm});
            skPoint(sketch, "E49", {"position": v(21.5, -1.17) * mm});
            skLineSegment(sketch, "E50", {"start": v(21.5, 3.5) * mm, "end": v(21.5, 1.17) * mm});
            skLineSegment(sketch, "E51", {"start": v(21.5, -1.17) * mm, "end": v(21.5, 1.17) * mm});
            skLineSegment(sketch, "E52", {"start": v(21.5, -1.17) * mm, "end": v(21.5, -3.5) * mm});
            skLineSegment(sketch, "E53", {"start": v(21.5, 1.17) * mm, "end": v(16.5, 1.17) * mm});
            skLineSegment(sketch, "E54", {"start": v(21.5, -1.17) * mm, "end": v(16.5, -1.17) * mm});
            skPoint(sketch, "E55", {"position": v(19, 3.5) * mm});
            skPoint(sketch, "E56", {"position": v(19, -3.5) * mm});
            skLineSegment(sketch, "E57", {"start": v(19, 3.5) * mm, "end": v(19, -3.5) * mm});
            skPoint(sketch, "E58", {"position": v(17.75, 2.25) * mm});
            skLineSegment(sketch, "E59", {"start": v(17.75, 2.25) * mm, "end": v(17.75, 3.5) * mm, "construction": true});
            skLineSegment(sketch, "E60", {"start": v(17.75, 2.25) * mm, "end": v(16.5, 2.25) * mm, "construction": true});
            skLineSegment(sketch, "E61", {"start": v(17.75, 2.25) * mm, "end": v(19, 2.25) * mm, "construction": true});
            skLineSegment(sketch, "E62", {"start": v(17.75, 2.25) * mm, "end": v(17.75, 1.17) * mm, "construction": true});
            skLineSegment(sketch, "E63.bottom", {"start": v(18.07, 2.57) * mm, "end": v(17.43, 2.57) * mm});
            skLineSegment(sketch, "E63.top", {"start": v(18.07, 1.93) * mm, "end": v(17.43, 1.93) * mm});
            skLineSegment(sketch, "E63.left", {"start": v(18.07, 2.57) * mm, "end": v(18.07, 1.93) * mm});
            skLineSegment(sketch, "E63.right", {"start": v(17.43, 2.57) * mm, "end": v(17.43, 1.93) * mm});
            skLineSegment(sketch, "E64.1.0.0", {"start": v(20.57, 2.57) * mm, "end": v(20.57, 1.93) * mm});
            skLineSegment(sketch, "E64.1.0.1", {"start": v(20.57, 2.57) * mm, "end": v(19.93, 2.57) * mm});
            skLineSegment(sketch, "E64.1.0.2", {"start": v(19.93, 2.57) * mm, "end": v(19.93, 1.93) * mm});
            skLineSegment(sketch, "E64.1.0.3", {"start": v(20.57, 1.93) * mm, "end": v(19.93, 1.93) * mm});
            skPoint(sketch, "E65", {"position": v(20.25, 2.25) * mm});
            skLineSegment(sketch, "E66", {"start": v(19, 2.25) * mm, "end": v(20.25, 2.25) * mm, "construction": true});
            skLineSegment(sketch, "E67", {"start": v(20.25, 2.25) * mm, "end": v(21.5, 2.25) * mm, "construction": true});
            skLineSegment(sketch, "E68", {"start": v(20.25, 3.5) * mm, "end": v(20.25, 2.25) * mm, "construction": true});
            skPoint(sketch, "E68.startSnap0", {"position": v(20.25, 2.57) * mm});
            skLineSegment(sketch, "E69", {"start": v(20.25, 1.17) * mm, "end": v(20.25, 2.25) * mm, "construction": true});
            skPoint(sketch, "E70", {"position": v(21.5, 0) * mm});
            skPoint(sketch, "E71.0.1.0", {"position": v(20.25, 0) * mm});
            skLineSegment(sketch, "E71.0.1.1", {"start": v(20.57, 0.32) * mm, "end": v(20.57, -0.32) * mm});
            skLineSegment(sketch, "E71.0.1.2", {"start": v(20.57, 0.32) * mm, "end": v(19.93, 0.32) * mm});
            skLineSegment(sketch, "E71.0.1.3", {"start": v(19.93, 0.32) * mm, "end": v(19.93, -0.32) * mm});
            skLineSegment(sketch, "E71.0.1.4", {"start": v(20.57, -0.32) * mm, "end": v(19.93, -0.32) * mm});
            skLineSegment(sketch, "E71.0.1.5", {"start": v(18.07, 0.32) * mm, "end": v(18.07, -0.32) * mm});
            skLineSegment(sketch, "E71.0.1.6", {"start": v(18.07, -0.32) * mm, "end": v(17.43, -0.32) * mm});
            skLineSegment(sketch, "E71.0.1.7", {"start": v(17.43, 0.32) * mm, "end": v(17.43, -0.32) * mm});
            skLineSegment(sketch, "E71.0.1.8", {"start": v(18.07, 0.32) * mm, "end": v(17.43, 0.32) * mm});
            skPoint(sketch, "E71.0.2.0", {"position": v(20.25, -2.25) * mm});
            skLineSegment(sketch, "E71.0.2.1", {"start": v(20.57, -1.93) * mm, "end": v(20.57, -2.57) * mm});
            skLineSegment(sketch, "E71.0.2.2", {"start": v(20.57, -1.93) * mm, "end": v(19.93, -1.93) * mm});
            skLineSegment(sketch, "E71.0.2.3", {"start": v(19.93, -1.93) * mm, "end": v(19.93, -2.57) * mm});
            skLineSegment(sketch, "E71.0.2.4", {"start": v(20.57, -2.57) * mm, "end": v(19.93, -2.57) * mm});
            skLineSegment(sketch, "E71.0.2.5", {"start": v(18.07, -1.93) * mm, "end": v(18.07, -2.57) * mm});
            skLineSegment(sketch, "E71.0.2.6", {"start": v(18.07, -2.57) * mm, "end": v(17.43, -2.57) * mm});
            skLineSegment(sketch, "E71.0.2.7", {"start": v(17.43, -1.93) * mm, "end": v(17.43, -2.57) * mm});
            skLineSegment(sketch, "E71.0.2.8", {"start": v(18.07, -1.93) * mm, "end": v(17.43, -1.93) * mm});
            skLineSegment(sketch, "E71.direction1", {"start": v(20.25, 2.25) * mm, "end": v(31.55, 2.25) * mm, "construction": true});
            skLineSegment(sketch, "E71.direction2", {"start": v(20.25, 2.25) * mm, "end": v(20.25, 0) * mm, "construction": true});
            skSolve(sketch);
        }
        {
            var Q0;
            Q0=makeQuery(id+"F11.imprint","IMPRINT",FACE,{"disambiguationData":[TD([[makeQuery(id+"F11.imprint","IMPRINT",EDGE,{"derivedFrom":sQuery(id+"F11.wireOp",EDGE,"E71.0.2.1")}),-1.0]])]});
            var Q1;
            Q1=makeQuery(id+"F11.imprint","IMPRINT",FACE,{"disambiguationData":[TD([[makeQuery(id+"F11.imprint","IMPRINT",EDGE,{"derivedFrom":sQuery(id+"F11.wireOp",EDGE,"E71.0.2.5")}),-1.0]])]});
            var Q2;
            Q2=makeQuery(id+"F11.imprint","IMPRINT",FACE,{"disambiguationData":[TD([[makeQuery(id+"F11.imprint","IMPRINT",EDGE,{"derivedFrom":sQuery(id+"F11.wireOp",EDGE,"E71.0.1.5")}),-1.0]])]});
            var Q3;
            Q3=makeQuery(id+"F11.imprint","IMPRINT",FACE,{"disambiguationData":[TD([[makeQuery(id+"F11.imprint","IMPRINT",EDGE,{"derivedFrom":sQuery(id+"F11.wireOp",EDGE,"E71.0.1.1")}),-1.0]])]});
            var Q4;
            Q4=makeQuery(id+"F11.imprint","IMPRINT",FACE,{"disambiguationData":[TD([[makeQuery(id+"F11.imprint","IMPRINT",EDGE,{"derivedFrom":sQuery(id+"F11.wireOp",EDGE,"E64.1.0.0")}),-1.0]])]});
            var Q5;
            Q5=makeQuery(id+"F11.imprint","IMPRINT",FACE,{"disambiguationData":[TD([[makeQuery(id+"F11.imprint","IMPRINT",EDGE,{"derivedFrom":sQuery(id+"F11.wireOp",EDGE,"E63.bottom")}),1.0]])]});
            extrude(context, id + "F12", {"entities" : qUnion([Q0, Q1, Q2, Q3, Q4, Q5]), "operationType" : NewBodyOperationType.ADD, "depth" : 8 * mm});
        }
        {
            var Q0;
            Q0=makeQuery(id+"F3.opExtrude","SWEPT_EDGE",EDGE,{"disambiguationData":[OSD([sQuery(id+"F0.wireOp",EDGE,"E0.left"),sQuery(id+"F0.wireOp",EDGE,"E7.bottom"),sQuery(id+"F0.wireOp",EDGE,"E7.left")])]});
            var Q1;
            Q1=makeQuery(id+"F3.opExtrude","SWEPT_EDGE",EDGE,{"disambiguationData":[OSD([sQuery(id+"F0.wireOp",EDGE,"E7.bottom"),sQuery(id+"F0.wireOp",EDGE,"E7.right")])]});
            var Q2;
            Q2=makeQuery(id+"F3.opExtrude","SWEPT_EDGE",EDGE,{"disambiguationData":[OSD([sQuery(id+"F0.wireOp",EDGE,"E0.left"),sQuery(id+"F0.wireOp",EDGE,"E7.top"),sQuery(id+"F0.wireOp",EDGE,"E7.left")])]});
            var Q3;
            Q3=makeQuery(id+"F3.opExtrude","SWEPT_EDGE",EDGE,{"disambiguationData":[OSD([sQuery(id+"F0.wireOp",EDGE,"E7.top"),sQuery(id+"F0.wireOp",EDGE,"E7.right")])]});
            chamfer(context, id + "F13", {"entities" : qUnion([Q0, Q1, Q2, Q3]), "width" : 0.4 * mm, "tangentPropagation" : true});
        }
    });
